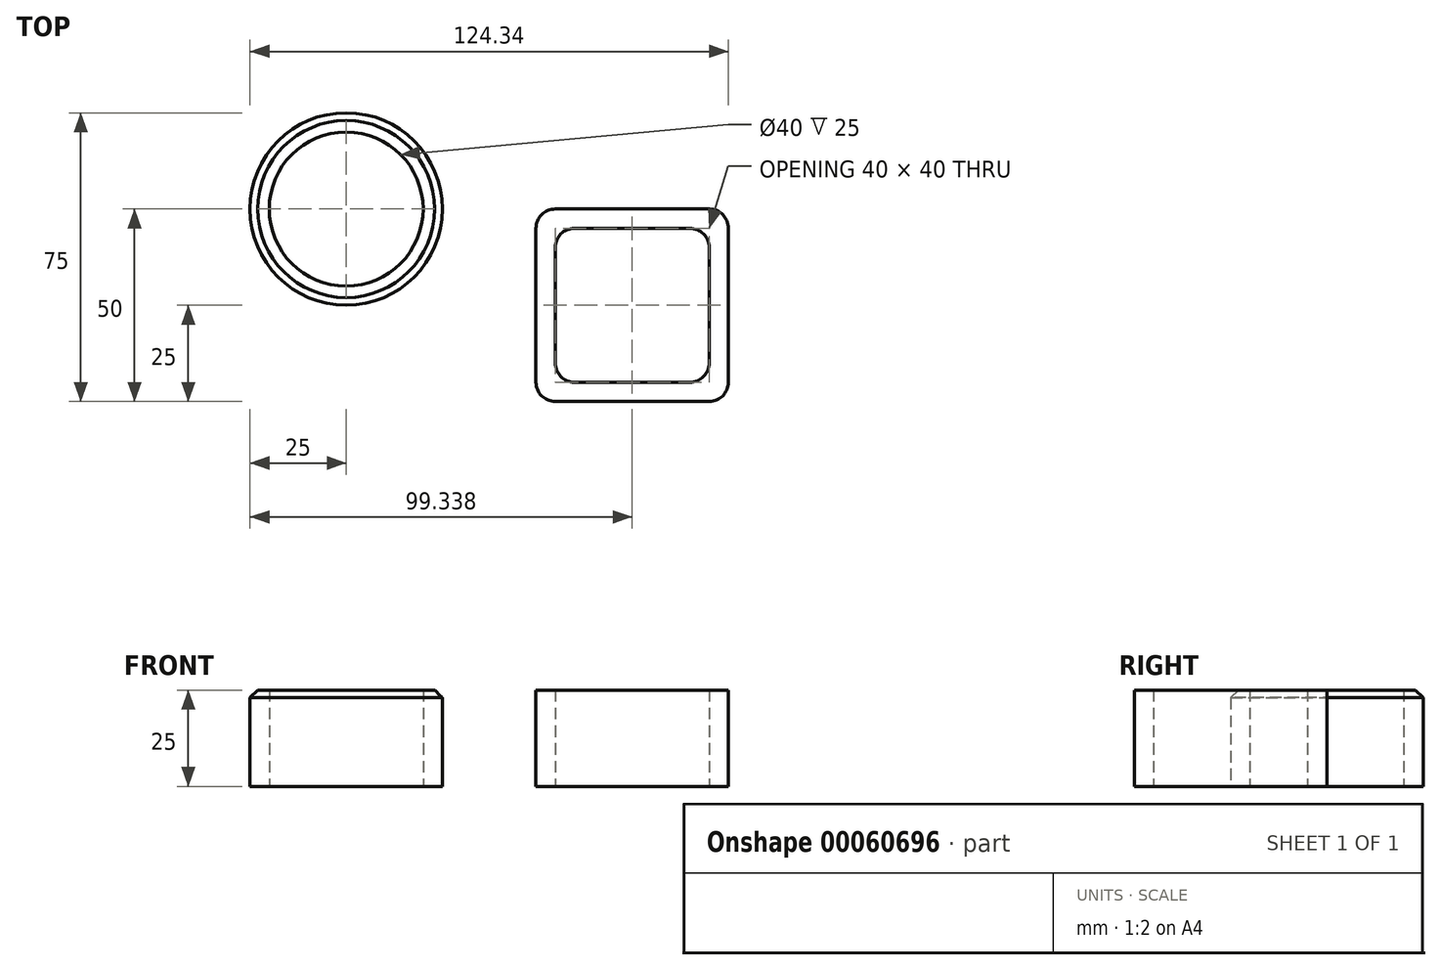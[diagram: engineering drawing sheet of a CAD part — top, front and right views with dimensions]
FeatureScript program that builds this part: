
annotation { "Feature Type Name" : "Feature", "Feature Type Description" : "" }
export const myFeature = defineFeature(function(context is Context, id is Id, definition is map)
    precondition{}
    {
        {
            var Q0;
            Q0=qCreatedBy(makeId("Top.planeOp"),FACE);
            var sketch = newSketch(context, id + "F0", { "sketchPlane" : qUnion([Q0])});
            skCircle(sketch, "E0", {"center": v(0, 0) * mm, "radius": 25 * mm});
            skCircle(sketch, "E1", {"center": v(0, 0) * mm, "radius": 20 * mm});
            skSolve(sketch);
        }
        {
            var Q0;
            Q0 = qSketchRegion(id + "F0", true);
            extrude(context, id + "F1", {"entities" : qUnion([Q0]), "depth" : 25 * mm});
        }
        {
            var Q0;
            Q0=qCreatedBy(makeId("Top.planeOp"),FACE);
            var sketch = newSketch(context, id + "F2", { "sketchPlane" : qUnion([Q0])});
            skLineSegment(sketch, "E2.bottom", {"start": v(49.34, 0) * mm, "end": v(99.34, 0) * mm});
            skLineSegment(sketch, "E2.top", {"start": v(49.34, -50) * mm, "end": v(99.34, -50) * mm});
            skLineSegment(sketch, "E2.left", {"start": v(49.34, 0) * mm, "end": v(49.34, -50) * mm});
            skLineSegment(sketch, "E2.right", {"start": v(99.34, 0) * mm, "end": v(99.34, -50) * mm});
            skLineSegment(sketch, "E3.bottom", {"start": v(54.34, -5) * mm, "end": v(94.34, -5) * mm});
            skLineSegment(sketch, "E3.top", {"start": v(54.34, -45) * mm, "end": v(94.34, -45) * mm});
            skLineSegment(sketch, "E3.left", {"start": v(54.34, -5) * mm, "end": v(54.34, -45) * mm});
            skLineSegment(sketch, "E3.right", {"start": v(94.34, -5) * mm, "end": v(94.34, -45) * mm});
            skSolve(sketch);
        }
        {
            var Q0;
            Q0 = qSketchRegion(id + "F2", true);
            extrude(context, id + "F3", {"entities" : qUnion([Q0]), "depth" : 25 * mm});
        }
        {
            var Q0;
            Q0=makeQuery(id+"F3.opExtrude","SWEPT_EDGE",EDGE,{"disambiguationData":[OSD([sQuery(id+"F2.wireOp",EDGE,"E3.bottom"),sQuery(id+"F2.wireOp",EDGE,"E3.left")])]});
            var Q1;
            Q1=makeQuery(id+"F3.opExtrude","SWEPT_EDGE",EDGE,{"disambiguationData":[OSD([sQuery(id+"F2.wireOp",EDGE,"E3.top"),sQuery(id+"F2.wireOp",EDGE,"E3.left")])]});
            var Q2;
            Q2=makeQuery(id+"F3.opExtrude","SWEPT_EDGE",EDGE,{"disambiguationData":[OSD([sQuery(id+"F2.wireOp",EDGE,"E3.bottom"),sQuery(id+"F2.wireOp",EDGE,"E3.right")])]});
            var Q3;
            Q3=makeQuery(id+"F3.opExtrude","SWEPT_EDGE",EDGE,{"disambiguationData":[OSD([sQuery(id+"F2.wireOp",EDGE,"E3.top"),sQuery(id+"F2.wireOp",EDGE,"E3.right")])]});
            var Q4;
            Q4=makeQuery(id+"F3.opExtrude","SWEPT_EDGE",EDGE,{"disambiguationData":[OSD([sQuery(id+"F2.wireOp",EDGE,"E2.bottom"),sQuery(id+"F2.wireOp",EDGE,"E2.left")])]});
            var Q5;
            Q5=makeQuery(id+"F3.opExtrude","SWEPT_EDGE",EDGE,{"disambiguationData":[OSD([sQuery(id+"F2.wireOp",EDGE,"E2.bottom"),sQuery(id+"F2.wireOp",EDGE,"E2.right")])]});
            var Q6;
            Q6=makeQuery(id+"F3.opExtrude","SWEPT_EDGE",EDGE,{"disambiguationData":[OSD([sQuery(id+"F2.wireOp",EDGE,"E2.top"),sQuery(id+"F2.wireOp",EDGE,"E2.left")])]});
            var Q7;
            Q7=makeQuery(id+"F3.opExtrude","SWEPT_EDGE",EDGE,{"disambiguationData":[OSD([sQuery(id+"F2.wireOp",EDGE,"E2.top"),sQuery(id+"F2.wireOp",EDGE,"E2.right")])]});
            fillet(context, id + "F4", {"entities" : qUnion([Q0, Q1, Q2, Q3, Q4, Q5, Q6, Q7]), "radius" : 5 * mm, "tangentPropagation" : true, "allowEdgeOverflow" : false});
        }
        {
            var Q0;
            Q0=makeQuery(id+"F1.opExtrude","CAP_EDGE",EDGE,{"disambiguationData":[OSD([sQuery(id+"F0.wireOp",EDGE,"E0")])],"isStart":false});
            chamfer(context, id + "F5", {"entities" : qUnion([Q0]), "width" : 2 * mm, "tangentPropagation" : true});
        }
    });
